# Revit family: Legrand armoire XL3 HP 6300
name_source: partatom
category: Modèles génériques
units: mm (PartAtom-declared; Revit-internal decimal feet)

## family parameters
Basée sur le plan de construction = Non
Conserver l'orientation des annotations = Non
Cote de connecteur circulaire = Utiliser le diamètre
Couper avec des vides une fois chargée = Non
Numéro OmniClass = 23.80.30.11.17
Partagée = Non
Peut héberger une armature = Non
Repère de localisation dans la pièce = Non
Titre OmniClass = Distribution Boards and Control Panels
Toujours verticalement = Oui
Type d'élément = Normal

## types (2) — shared parameters
Conditions Générale d'Utilisation = https://assets.legrand.com
Fabricant = legrand
Hauteur socle = 100 mm  [stored 0.328084 ft]
RAL = 7035
zero-valued in all types: Elévation par défaut

## per-type parameters (varying)
| type | Assemblable | Autonome | Hauteur poignée | URL |
| Legrand armoire autonome métal XL3 HP 6300 | Non | Oui | 260 mm  [stored 0.853018 ft] |  |
| Legrand armoire assemblable métal XL3 HP 6300 | Oui | Non | 120 mm  [stored 0.393701 ft] | https://www.legrand.fr |

note: [stored X ft] marks values corroborated as IEEE doubles in the binary element streams (Revit-internal decimal feet)
